# Revit family: Indoor_Pendant Lamp_Santa&Cole_Arne S Domus
name_source: partatom
category: Luminarias
revit_build: Autodesk Revit 2018 (Build: 20190510_1515(x64)
units: mm (PartAtom-declared; Revit-internal decimal feet)

## family parameters
Anfitrión = Cara
Compartido = No
Corte con vacíos al cargar = No
Cota de conector redondo = Diámetro de uso
Origen de luz = Sí
Punto de cálculo de habitación = No
Tipo de pieza = Normal

## types (4) — shared parameters
Archivo de red fotométrica = ARD1x.IES
Assembly Instructions - CE = https://www.santacole.com
Assembly Instructions - UL = https://www.santacole.com
Cambio de temperatura de color de luz atenuada = <Ninguno>
Elevación por defecto = 1219 mm
Energy Label = https://www.santacole.com
Fabricante = Santa & Cole
Filtro de color = 16777215
Manufacturer website = http://www.santacole.com
Technical Information = https://www.santacole.com
URL = https://www.santacole.com
Voltaje (90-305 V) = 220 V
Ángulo de inclinación = -90.00°

## per-type parameters (varying)
| type | Carga aparente | Code | Lampshade Material | Load | Modelo |
| Arne S Domus - S&C White | 33 W | ARD1x | Santa&Cole - White Matte Finish | 33 W | Arne Domus |
| Arne S Domus - Aluminium Grey | 33 W | ARD1x | Santa & Cole - Aluminium | 33 W | Arne Domus |
| Arne S Domus - Dark Green | 28 W | ARSD1x | Santa & Cole - Dark Green | 28 W | Arne S Domus |
| Arne S Domus - Mustard | 33 W | ARD1x | Santa & Cole - Mustard | 33 W | Arne Domus |

## geometry (parser evidence)
native form markers: Blend x2, Sweep x3
no freeform markers — native parametric forms only
